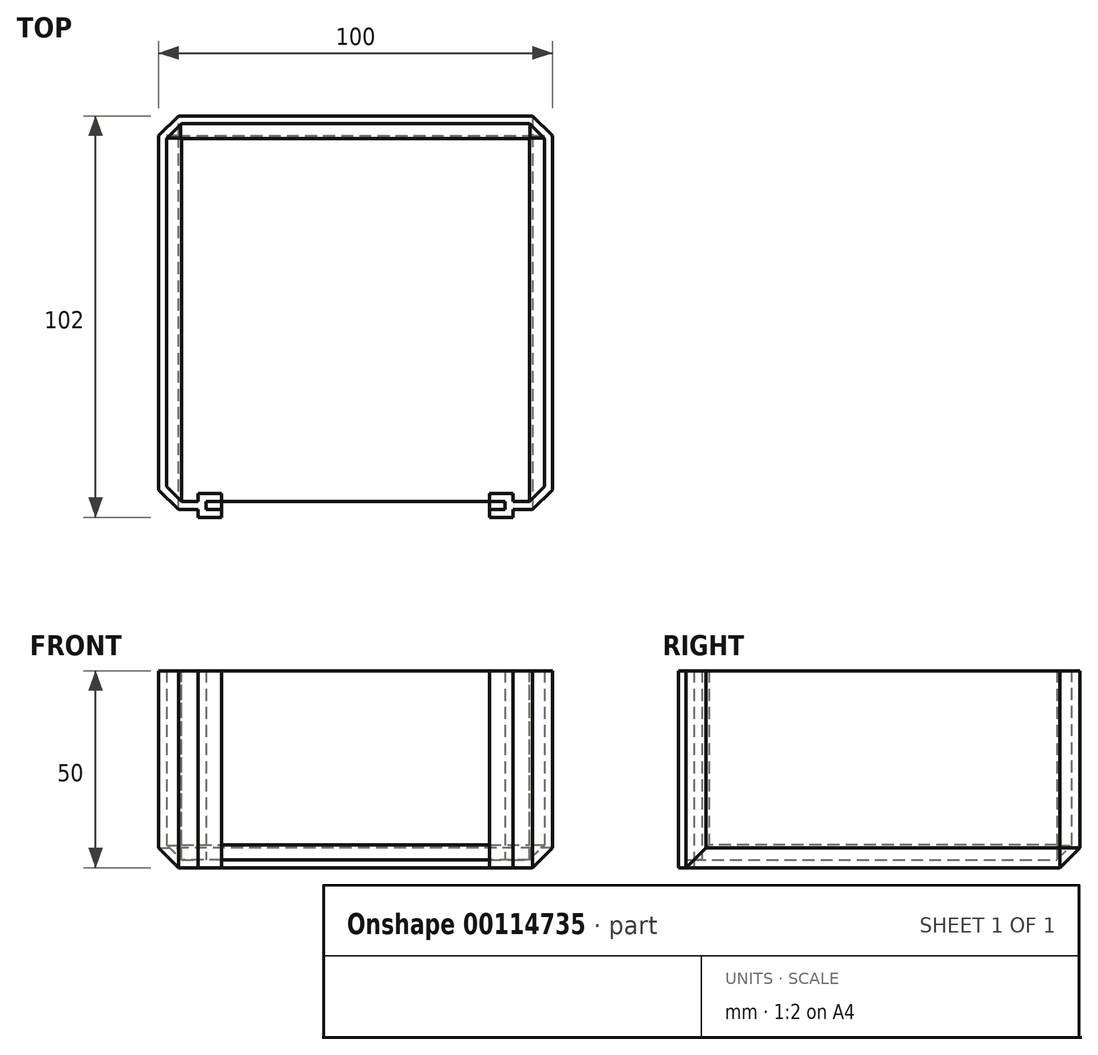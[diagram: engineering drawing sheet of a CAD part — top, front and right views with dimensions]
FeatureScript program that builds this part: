
annotation { "Feature Type Name" : "Feature", "Feature Type Description" : "" }
export const myFeature = defineFeature(function(context is Context, id is Id, definition is map)
    precondition{}
    {
        {
            var Q0;
            Q0=qCreatedBy(makeId("Front.planeOp"),FACE);
            var sketch = newSketch(context, id + "F0", { "sketchPlane" : qUnion([Q0])});
            skLineSegment(sketch, "E0.bottom", {"start": v(0, 0) * mm, "end": v(100, 0) * mm});
            skLineSegment(sketch, "E0.top", {"start": v(0, 50) * mm, "end": v(100, 50) * mm});
            skLineSegment(sketch, "E0.left", {"start": v(0, 0) * mm, "end": v(0, 50) * mm});
            skLineSegment(sketch, "E0.right", {"start": v(100, 0) * mm, "end": v(100, 50) * mm});
            skSolve(sketch);
        }
        {
            var Q0;
            Q0=makeQuery(id+"F0.imprint","IMPRINT",FACE,{"disambiguationData":[TD([[makeQuery(id+"F0.imprint","IMPRINT",EDGE,{"derivedFrom":sQuery(id+"F0.wireOp",EDGE,"E0.bottom")}),1.0]])]});
            extrude(context, id + "F1", {"entities" : qUnion([Q0]), "depth" : 100 * mm});
        }
        {
            var Q0;
            Q0=makeQuery(id+"F1.opExtrude","CAP_EDGE",EDGE,{"disambiguationData":[OSD([sQuery(id+"F0.wireOp",EDGE,"E0.bottom")])],"isStart":true});
            var Q1;
            Q1=makeQuery(id+"F1.opExtrude","SWEPT_EDGE",EDGE,{"disambiguationData":[OSD([sQuery(id+"F0.wireOp",EDGE,"E0.bottom"),sQuery(id+"F0.wireOp",EDGE,"E0.left")])]});
            var Q2;
            Q2=makeQuery(id+"F1.opExtrude","SWEPT_EDGE",EDGE,{"disambiguationData":[OSD([sQuery(id+"F0.wireOp",EDGE,"E0.bottom"),sQuery(id+"F0.wireOp",EDGE,"E0.right")])]});
            var Q3;
            Q3=makeQuery(id+"F1.opExtrude","CAP_EDGE",EDGE,{"disambiguationData":[OSD([sQuery(id+"F0.wireOp",EDGE,"E0.left")])],"isStart":false});
            var Q4;
            Q4=makeQuery(id+"F1.opExtrude","CAP_EDGE",EDGE,{"disambiguationData":[OSD([sQuery(id+"F0.wireOp",EDGE,"E0.right")])],"isStart":false});
            var Q5;
            Q5=makeQuery(id+"F1.opExtrude","CAP_EDGE",EDGE,{"disambiguationData":[OSD([sQuery(id+"F0.wireOp",EDGE,"E0.right")])],"isStart":true});
            var Q6;
            Q6=makeQuery(id+"F1.opExtrude","CAP_EDGE",EDGE,{"disambiguationData":[OSD([sQuery(id+"F0.wireOp",EDGE,"E0.left")])],"isStart":true});
            chamfer(context, id + "F2", {"entities" : qUnion([Q0, Q1, Q2, Q3, Q4, Q5, Q6]), "width" : 5 * mm, "tangentPropagation" : true});
        }
        {
            var Q0;
            Q0=makeQuery(id+"F1.opExtrude","SWEPT_FACE",FACE,{"disambiguationData":[OSD([sQuery(id+"F0.wireOp",EDGE,"E0.top")])]});
            shell(context, id + "F3", {"entities" : qUnion([Q0]), "thickness" : 2 * mm});
        }
        {
            var Q0;
            Q0=makeQuery(id+"F1.opExtrude","SWEPT_FACE",FACE,{"disambiguationData":[OSD([sQuery(id+"F0.wireOp",EDGE,"E0.top")])]});
            var sketch = newSketch(context, id + "F4", { "sketchPlane" : qUnion([Q0])});
            skLineSegment(sketch, "E1", {"start": v(10, -98) * mm, "end": v(10, -100) * mm});
            skLineSegment(sketch, "E2", {"start": v(10, -100) * mm, "end": v(90, -100) * mm});
            skLineSegment(sketch, "E3", {"start": v(90, -100) * mm, "end": v(90, -98) * mm});
            skLineSegment(sketch, "E4", {"start": v(90, -98) * mm, "end": v(10, -98) * mm});
            skSolve(sketch);
        }
        {
            var Q0;
            Q0=makeQuery(id+"F4.imprint","IMPRINT",FACE,{"disambiguationData":[TD([[makeQuery(id+"F4.imprint","IMPRINT",EDGE,{"derivedFrom":sQuery(id+"F4.wireOp",EDGE,"E1")}),1.0]])]});
            extrude(context, id + "F5", {"entities" : qUnion([Q0]), "operationType" : NewBodyOperationType.REMOVE, "oppositeDirection" : true, "depth" : 50 * mm});
        }
        {
            var Q0;
            Q0=makeQuery(id+"F1.opExtrude","SWEPT_FACE",FACE,{"disambiguationData":[OSD([sQuery(id+"F0.wireOp",EDGE,"E0.bottom")])]});
            var sketch = newSketch(context, id + "F6", { "sketchPlane" : qUnion([Q0])});
            skLineSegment(sketch, "E5", {"start": v(10, 102) * mm, "end": v(10, 96) * mm});
            skPoint(sketch, "E5.endSnap0", {"position": v(10, 99) * mm});
            skLineSegment(sketch, "E6", {"start": v(10, 96) * mm, "end": v(16, 96) * mm});
            skLineSegment(sketch, "E7", {"start": v(16, 96) * mm, "end": v(16, 98) * mm});
            skLineSegment(sketch, "E8", {"start": v(16, 98) * mm, "end": v(12, 98) * mm});
            skLineSegment(sketch, "E9", {"start": v(12, 98) * mm, "end": v(12, 100) * mm});
            skLineSegment(sketch, "E10", {"start": v(12, 100) * mm, "end": v(16, 100) * mm});
            skLineSegment(sketch, "E11", {"start": v(16, 100) * mm, "end": v(16, 102) * mm});
            skLineSegment(sketch, "E12", {"start": v(16, 102) * mm, "end": v(10, 102) * mm});
            skSolve(sketch);
        }
        {
            var Q0;
            {var subQ0=sQuery(id+"F6.wireOp",EDGE,"E9");Q0=makeQuery(id+"F6.imprint","IMPRINT",FACE,{"disambiguationData":[TD([[makeQuery(id+"F6.imprint","IMPRINT",EDGE,{"derivedFrom":subQ0}),1.0]])]});}
            var Q1;
            {var subQ1=sQuery(id+"F6.wireOp",EDGE,"E6");Q1=makeQuery(id+"F6.imprint","IMPRINT",FACE,{"disambiguationData":[TD([[makeQuery(id+"F6.imprint","IMPRINT",EDGE,{"derivedFrom":subQ1}),1.0]])]});}
            extrude(context, id + "F7", {"entities" : qUnion([Q0, Q1]), "operationType" : NewBodyOperationType.ADD, "oppositeDirection" : true, "depth" : 50 * mm});
        }
        {
            var Q0;
            Q0=makeQuery(id+"F7.opExtrude","SWEPT_FACE",FACE,{"disambiguationData":[OSD([sQuery(id+"F6.wireOp",EDGE,"E9")])]});
            var sketch = newSketch(context, id + "F8", { "sketchPlane" : qUnion([Q0])});
            skLineSegment(sketch, "E13.bottom", {"start": v(-100, 0) * mm, "end": v(-98, 0) * mm});
            skLineSegment(sketch, "E13.top", {"start": v(-100, 2) * mm, "end": v(-98, 2) * mm});
            skLineSegment(sketch, "E13.left", {"start": v(-100, 0) * mm, "end": v(-100, 2) * mm});
            skLineSegment(sketch, "E13.right", {"start": v(-98, 0) * mm, "end": v(-98, 2) * mm});
            skSolve(sketch);
        }
        {
            var Q0;
            Q0=makeQuery(id+"F8.imprint","IMPRINT",FACE,{"disambiguationData":[TD([[makeQuery(id+"F8.imprint","IMPRINT",EDGE,{"derivedFrom":sQuery(id+"F8.wireOp",EDGE,"E13.bottom")}),-1.0]])]});
            extrude(context, id + "F9", {"entities" : qUnion([Q0]), "operationType" : NewBodyOperationType.ADD, "depth" : 4 * mm});
        }
        {
            var Q0;
            Q0=makeQuery(id+"F9.boolean.opBoolean","MERGE",FACE,{"derivedFrom":[makeQuery(id+"F7.boolean.opBoolean","MERGE",FACE,{"derivedFrom":[makeQuery(id+"F1.opExtrude","SWEPT_FACE",FACE,{"disambiguationData":[OSD([sQuery(id+"F0.wireOp",EDGE,"E0.bottom")])]}),makeQuery(id+"F7.opExtrude","CAP_FACE",FACE,{"disambiguationData":[OSD([sQuery(id+"F6.wireOp",EDGE,"E5"),sQuery(id+"F6.wireOp",EDGE,"E6"),sQuery(id+"F6.wireOp",EDGE,"E7"),sQuery(id+"F6.wireOp",EDGE,"E8"),sQuery(id+"F6.wireOp",EDGE,"E9"),sQuery(id+"F6.wireOp",EDGE,"E10"),sQuery(id+"F6.wireOp",EDGE,"E11"),sQuery(id+"F6.wireOp",EDGE,"E12")])],"isStart":true})]}),makeQuery(id+"F9.opExtrude","SWEPT_FACE",FACE,{"disambiguationData":[OSD([sQuery(id+"F8.wireOp",EDGE,"E13.bottom")])]})]});
            var sketch = newSketch(context, id + "F10", { "sketchPlane" : qUnion([Q0])});
            skLineSegment(sketch, "E14", {"start": v(90, 102) * mm, "end": v(90, 96) * mm});
            skLineSegment(sketch, "E15", {"start": v(90, 96) * mm, "end": v(84, 96) * mm});
            skLineSegment(sketch, "E16", {"start": v(84, 96) * mm, "end": v(84, 98) * mm});
            skLineSegment(sketch, "E17", {"start": v(84, 98) * mm, "end": v(88, 98) * mm});
            skLineSegment(sketch, "E18", {"start": v(88, 98) * mm, "end": v(88, 100) * mm});
            skLineSegment(sketch, "E19", {"start": v(88, 100) * mm, "end": v(84, 100) * mm});
            skLineSegment(sketch, "E20", {"start": v(84, 100) * mm, "end": v(84, 102) * mm});
            skLineSegment(sketch, "E21", {"start": v(84, 102) * mm, "end": v(90, 102) * mm});
            skSolve(sketch);
        }
        {
            var Q0;
            {var subQ0=sQuery(id+"F10.wireOp",EDGE,"E18");Q0=makeQuery(id+"F10.imprint","IMPRINT",FACE,{"disambiguationData":[TD([[makeQuery(id+"F10.imprint","IMPRINT",EDGE,{"derivedFrom":subQ0}),-1.0]])]});}
            var Q1;
            {var subQ1=sQuery(id+"F10.wireOp",EDGE,"E15");Q1=makeQuery(id+"F10.imprint","IMPRINT",FACE,{"disambiguationData":[TD([[makeQuery(id+"F10.imprint","IMPRINT",EDGE,{"derivedFrom":subQ1}),-1.0]])]});}
            extrude(context, id + "F11", {"entities" : qUnion([Q0, Q1]), "operationType" : NewBodyOperationType.ADD, "oppositeDirection" : true, "depth" : 50 * mm});
        }
        {
            var Q0;
            Q0=makeQuery(id+"F11.opExtrude","SWEPT_FACE",FACE,{"disambiguationData":[OSD([sQuery(id+"F10.wireOp",EDGE,"E18")])]});
            var sketch = newSketch(context, id + "F12", { "sketchPlane" : qUnion([Q0])});
            skLineSegment(sketch, "E22.bottom", {"start": v(98, 0) * mm, "end": v(100, 0) * mm});
            skLineSegment(sketch, "E22.top", {"start": v(98, 2) * mm, "end": v(100, 2) * mm});
            skLineSegment(sketch, "E22.left", {"start": v(98, 0) * mm, "end": v(98, 2) * mm});
            skLineSegment(sketch, "E22.right", {"start": v(100, 0) * mm, "end": v(100, 2) * mm});
            skSolve(sketch);
        }
        {
            var Q0;
            Q0=makeQuery(id+"F12.imprint","IMPRINT",FACE,{"disambiguationData":[TD([[makeQuery(id+"F12.imprint","IMPRINT",EDGE,{"derivedFrom":sQuery(id+"F12.wireOp",EDGE,"E22.bottom")}),1.0]])]});
            extrude(context, id + "F13", {"entities" : qUnion([Q0]), "operationType" : NewBodyOperationType.ADD, "depth" : 4 * mm});
        }
    });
